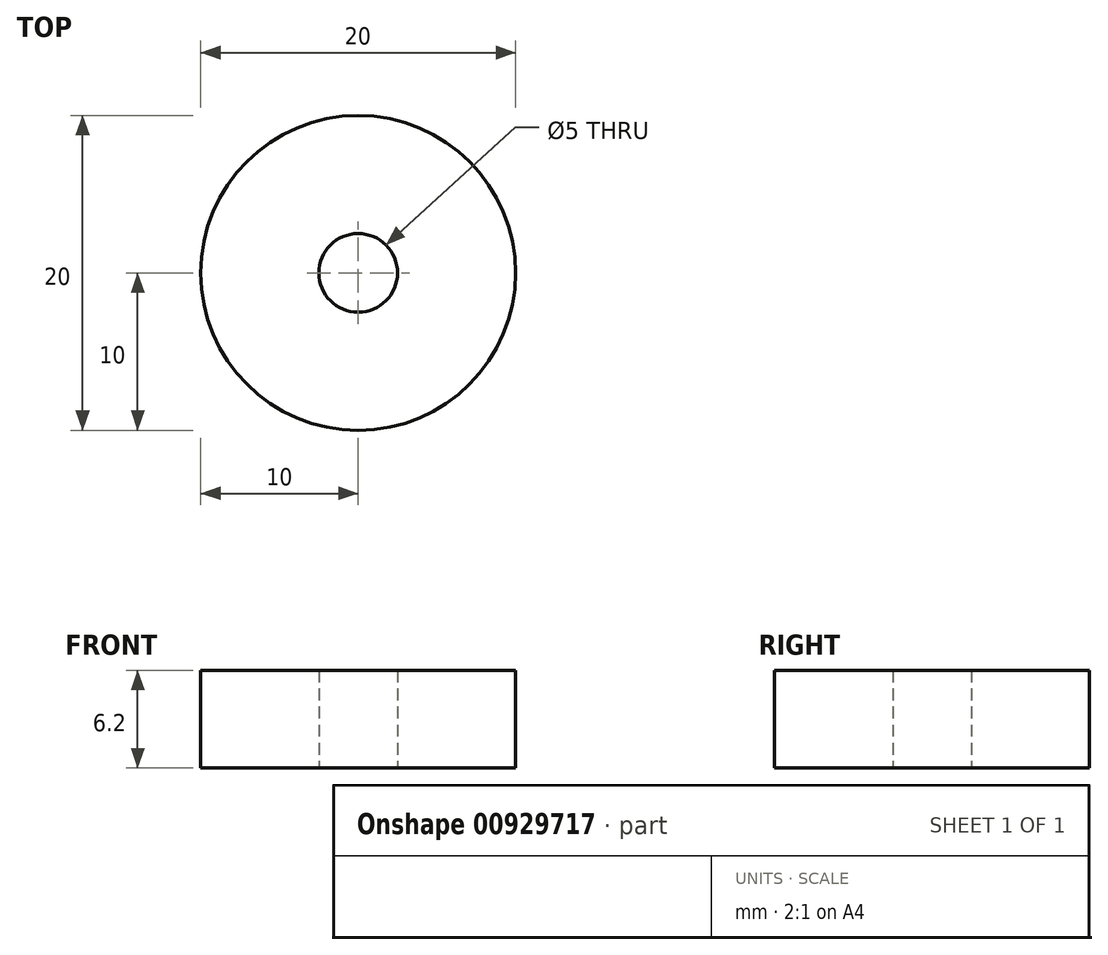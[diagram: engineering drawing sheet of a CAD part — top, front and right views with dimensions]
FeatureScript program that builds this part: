
annotation { "Feature Type Name" : "Feature", "Feature Type Description" : "" }
export const myFeature = defineFeature(function(context is Context, id is Id, definition is map)
    precondition{}
    {
        {
            var Q0;
            Q0=qCreatedBy(makeId("Top.planeOp"),FACE);
            var sketch = newSketch(context, id + "F0", { "sketchPlane" : qUnion([Q0])});
            skCircle(sketch, "E0", {"center": v(0, 0) * mm, "radius": 2.5 * mm});
            skCircle(sketch, "E1", {"center": v(0, 0) * mm, "radius": 10 * mm});
            skSolve(sketch);
        }
        {
            var Q0;
            Q0=makeQuery(id+"F0.imprint","IMPRINT",FACE,{"disambiguationData":[TD([[makeQuery(id+"F0.imprint","IMPRINT",EDGE,{"derivedFrom":sQuery(id+"F0.wireOp",EDGE,"E0")}),-1.0]])]});
            extrude(context, id + "F1", {"entities" : qUnion([Q0]), "depth" : 6.2 * mm, "offsetDistance" : 25 * mm});
        }
    });
